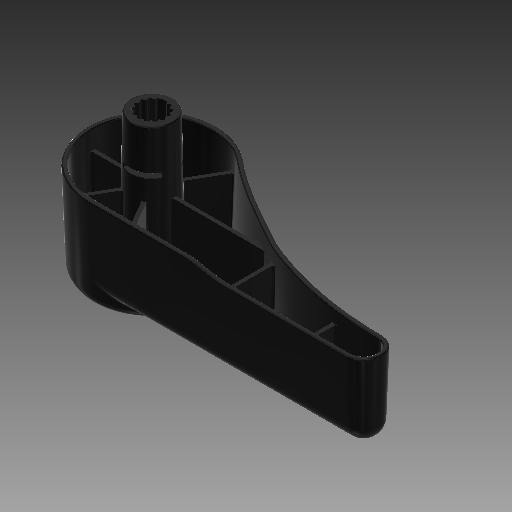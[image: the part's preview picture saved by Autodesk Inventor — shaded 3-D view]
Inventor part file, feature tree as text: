
AUTODESK INVENTOR PART (.ipt)
format: ipt  version: 2019 (Build 230136000, 136)  size: 1,675,264 bytes
history: native  units: mm
features: fillet x10, sketch x10, plane x7, extrude x5, projected_geometry x4, other x2, rib x2, loft x1, shell x1, pattern_circular x1
ambient origin geometry x8: Origin, YZ Plane, XZ Plane, XY Plane, X Axis, Y Axis, Z Axis, Center Point
bodies: Solid1 (feature_tree)
feature tree (43):
  plane  "Work Plane1"
  plane  "Work Plane2"
  plane  "Work Plane3"
  extrude  "Extrusion1"  Depth=20.0mm
  extrude  "Extrusion2"  Depth=140.0mm
  plane  "Work Plane6"
  loft  "Loft1"
  fillet  "Fillet1"  Radius=5.0mm
  fillet  "Fillet2"  [1 undecoded]
  fillet  "Fillet3"  Radius=8.0mm
  shell  "Shell1"  Thickness=3.0mm
  plane  "Work Plane7"
  extrude  "Extrusion3"  Depth=25.0mm
  extrude  "Extrusion4"  Depth=50.0mm
  fillet  "Fillet4"  Radius=3.0mm
  sketch  "Sketch13"  dims[d62=23.0mm d63=50.0mm d64=0.174533mm d65=3.0mm d66=70.0mm]
  other  "iFeature1:1"
  fillet  "Fillet5"  Radius=70.0mm
  plane  "Work Plane9"
  extrude  "Extrusion5"  Depth=50.0mm
  fillet  "Fillet6"  Radius=50.0mm
  fillet  "Fillet9"  Radius=30.0mm
  plane  "Work Plane10"
  rib  "Rib2"
  pattern_circular  "Circular Pattern1"  [2 undecoded]
  rib  "Rib3"
  fillet  "Fillet7"  Radius=4.537856mm
  fillet  "Fillet8"  Radius=4.537856mm
  fillet  "Fillet10"  Radius=4.537856mm
  sketch  "Sketch8"  dims[d0=60.0mm d1=-60.0mm d2=200.0mm d45=20.0mm]
  sketch  "Sketch9"  dims[d46=70.0mm d47=140.0mm]
  sketch  "Sketch10"  dims[d48=45.0mm d49=-0.349066mm d50=50.0mm d51=-0.349066mm d52=5.0mm d53=0.0mm d54=90.0deg]
  other  "Edges1"
  sketch  "Sketch11"  dims[d55=10.0mm d56=90.0deg d57=6.0mm d58=8.0mm d59=3.0mm]
  sketch  "Sketch12"  dims[d60=2.5mm d61=25.0mm]
  projected_geometry  "Projected Loop1"
  sketch  "Sketch19"  dims[d67=1.919862mm d68=50.0mm d69=50.0mm d70=0.0mm d71=30.0mm]
  sketch  "Sketch21"  dims[d173=16.04mm d174=1.02mm d175=4.18879mm d176=1.25mm d177=0.3mm d178=4.18879mm d179=1.25mm d180=0.3mm d181=285.0deg]
  sketch  "Sketch22"  dims[d183=4.537856mm d184=4.537856mm]
  sketch  "Sketch23"  dims[d185=4.537856mm d186=4.537856mm d187=4.537856mm d188=4.537856mm d189=4.537856mm d190=4.537856mm d191=4.537856mm d192=4.537856mm d193=4.537856mm d194=0.3mm d195=1.25mm d196=0.3mm d197=1.25mm d198=0.3mm d199=1.25mm d200=1.25mm d201=0.3mm d202=1.25mm d203=0.3mm d204=1.25mm d205=0.3mm d206=0.3mm d207=1.25mm d208=1.25mm d209=0.3mm d210=0.3mm d211=1.25mm d212=1.25mm d213=0.3mm d214=0.3mm d215=1.25mm d216=0.3mm d217=1.25mm d218=0.3mm d219=1.25mm d220=1.25mm d221=0.3mm d222=1.25mm d223=0.3mm d224=1.25mm d225=0.3mm d226=0.3mm d227=1.25mm d228=0.3mm d229=1.25mm d230=0.3mm d231=1.25mm d232=0.3mm d233=1.25mm d234=0.3mm d235=1.25mm d236=0.3mm d237=1.25mm d238=0.3mm d239=1.25mm d240=0.3mm d241=1.25mm d242=1.0mm d244=-23.85mm d245=4.363323mm d246=90.0deg d247=4.363323mm d248=90.0deg d249=2.0mm d250=0.0mm d251=0.5mm d252=-10.0mm d260=60.0mm d262=360.0deg d264=2.0mm d265=1.0mm d266=0.174533mm d267=60.0mm d268=360.0deg d270=115.0mm d271=70.0mm d272=2.0mm d273=1.0mm d274=0.174533mm d275=1.0mm d276=1.0mm d277=2.0mm d278=1.0mm]
  projected_geometry  "Project Cut Edges2"
  projected_geometry  "Project Cut Edges3"
  projected_geometry  "Project Cut Edges4"
note: 3 required parameter values undecoded (feature->parameter linkage not recoverable at this tier; creation-order binding heuristic only, values carry confidence <= 0.55)
